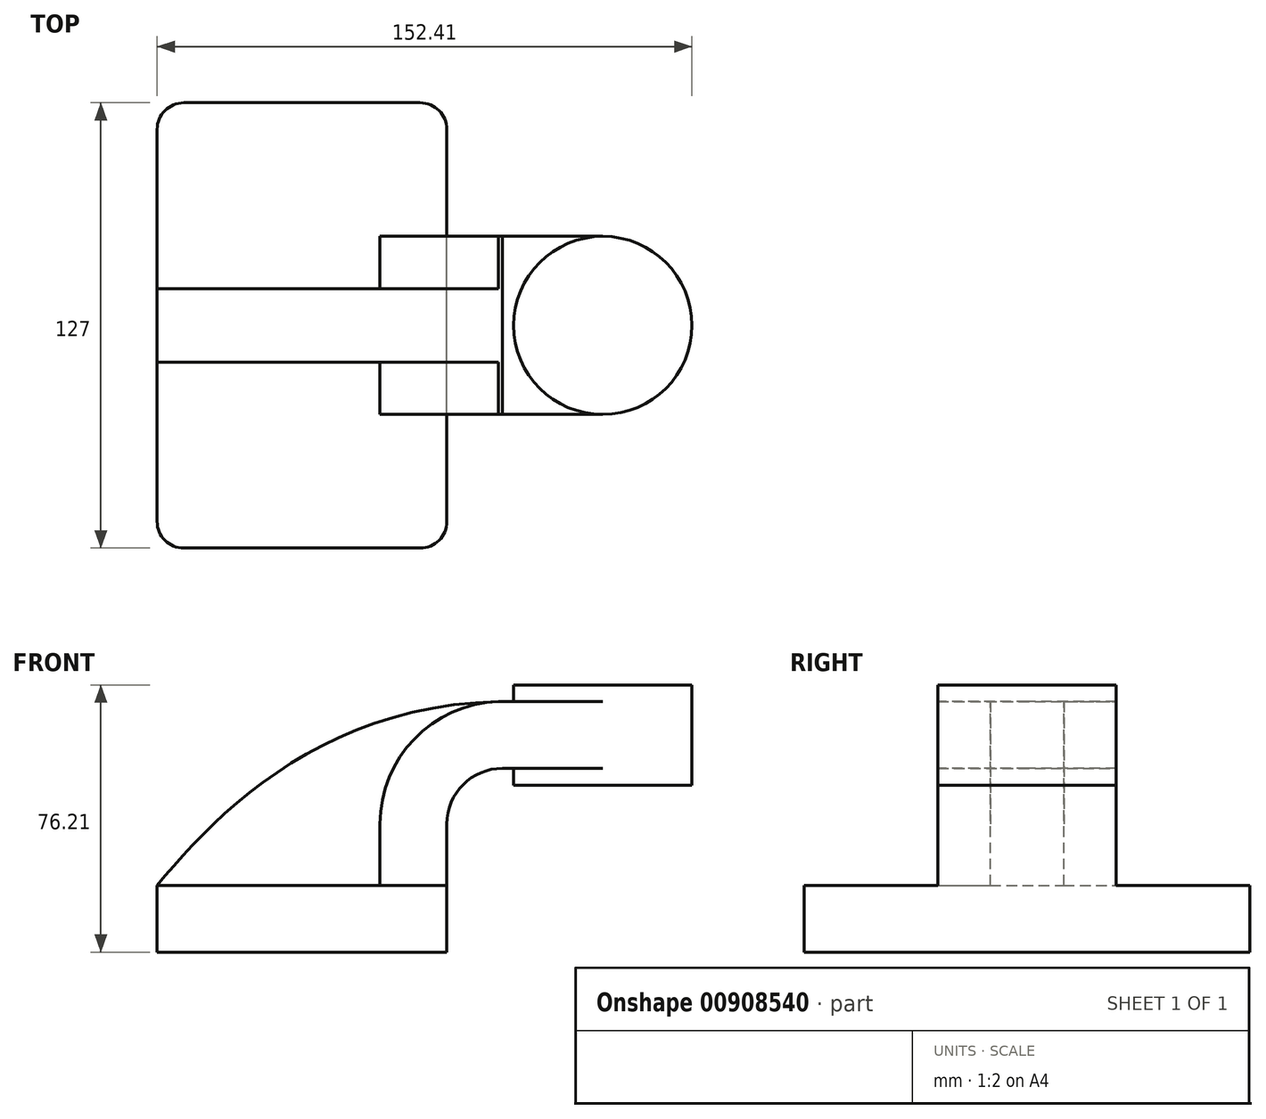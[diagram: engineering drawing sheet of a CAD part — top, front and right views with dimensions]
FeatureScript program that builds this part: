
annotation { "Feature Type Name" : "Feature", "Feature Type Description" : "" }
export const myFeature = defineFeature(function(context is Context, id is Id, definition is map)
    precondition{}
    {
        {
            var Q0;
            Q0=qCreatedBy(makeId("Front.planeOp"),FACE);
            var sketch = newSketch(context, id + "F0", { "sketchPlane" : qUnion([Q0])});
            skLineSegment(sketch, "E0.bottom", {"start": v(41.28, -9.52) * mm, "end": v(-41.28, -9.53) * mm});
            skLineSegment(sketch, "E0.top", {"start": v(41.27, 9.53) * mm, "end": v(-41.28, 9.53) * mm});
            skLineSegment(sketch, "E0.left", {"start": v(41.28, -9.52) * mm, "end": v(41.28, 9.53) * mm});
            skLineSegment(sketch, "E0.right", {"start": v(-41.28, -9.53) * mm, "end": v(-41.28, 9.53) * mm});
            skPoint(sketch, "E0.middle", {"position": v(0, 0) * mm});
            skLineSegment(sketch, "E1.bottom", {"start": v(60.32, 66.68) * mm, "end": v(111.12, 66.68) * mm});
            skLineSegment(sketch, "E1.top", {"start": v(60.32, 38.1) * mm, "end": v(111.12, 38.1) * mm});
            skLineSegment(sketch, "E1.left", {"start": v(60.32, 66.68) * mm, "end": v(60.32, 38.1) * mm});
            skLineSegment(sketch, "E1.right", {"start": v(111.12, 66.68) * mm, "end": v(111.12, 38.1) * mm});
            skPoint(sketch, "E1.middle", {"position": v(85.72, 52.39) * mm});
            skLineSegment(sketch, "E2", {"start": v(41.27, 9.53) * mm, "end": v(41.27, 27) * mm});
            skArc(sketch, "E3", {"start": v(57.15, 42.88) * mm, "mid": v(45.92, 38.23) * mm, "end": v(41.27, 27) * mm});
            skLineSegment(sketch, "E4", {"start": v(57.15, 42.88) * mm, "end": v(85.72, 42.88) * mm});
            skLineSegment(sketch, "E5.0", {"start": v(57.15, 61.93) * mm, "end": v(85.72, 61.93) * mm});
            skArc(sketch, "E5.1", {"start": v(57.15, 61.93) * mm, "mid": v(32.45, 51.7) * mm, "end": v(22.23, 27) * mm});
            skLineSegment(sketch, "E5.2", {"start": v(22.22, 9.53) * mm, "end": v(22.22, 27) * mm});
            skLineSegment(sketch, "E6", {"start": v(85.72, 38.1) * mm, "end": v(85.72, 66.68) * mm});
            skFitSpline(sketch, "E7", {"points": [v(-41.28, 9.52) * mm, v(57.15, 61.93) * mm], "startDerivative": vector(51.54, 62.19) * mm, "endDerivative": vector(153.31, 1.88) * mm});
            skSolve(sketch);
        }
        {
            var Q0;
            Q0=makeQuery(id+"F0.imprint","IMPRINT",FACE,{"disambiguationData":[TD([[makeQuery(id+"F0.imprint","IMPRINT",EDGE,{"derivedFrom":sQuery(id+"F0.wireOp",EDGE,"E0.bottom")}),-1.0]])]});
            extrude(context, id + "F1", {"entities" : qUnion([Q0]), "endBound" : BoundingType.SYMMETRIC, "depth" : 127 * mm, "offsetDistance" : 25.4 * mm});
        }
        {
            var Q0;
            {var subQ3=sQuery(id+"F0.wireOp",EDGE,"E5.2");Q0=makeQuery(id+"F0.imprint","IMPRINT",FACE,{"disambiguationData":[TD([[makeQuery(id+"F0.imprint","IMPRINT",EDGE,{"derivedFrom":subQ3}),1.0]])]});}
            extrude(context, id + "F2", {"entities" : qUnion([Q0]), "operationType" : NewBodyOperationType.ADD, "endBound" : BoundingType.SYMMETRIC, "depth" : 20.95 * mm, "offsetDistance" : 25.4 * mm});
        }
        {
            var Q0;
            {var subQ1=sQuery(id+"F0.wireOp",EDGE,"E2");Q0=makeQuery(id+"F0.imprint","IMPRINT",FACE,{"disambiguationData":[TD([[makeQuery(id+"F0.imprint","IMPRINT",EDGE,{"derivedFrom":subQ1}),1.0]])]});}
            var Q1;
            {var subQ0=sQuery(id+"F0.wireOp",EDGE,"E5.0");var subQ1=sQuery(id+"F0.wireOp",EDGE,"E1.left");var subQ2=makeQuery(id+"F0.imprint","INTERSECT",VERTEX,{"derivedFrom":[subQ1,subQ0]});Q1=makeQuery(id+"F0.imprint","IMPRINT",FACE,{"disambiguationData":[TD([[makeQuery(id+"F0.imprint","IMPRINT",EDGE,{"disambiguationData":[TD([[subQ2,-1.0]])],"derivedFrom":subQ1}),1.0]])]});}
            extrude(context, id + "F3", {"entities" : qUnion([Q0, Q1]), "operationType" : NewBodyOperationType.ADD, "endBound" : BoundingType.SYMMETRIC, "depth" : 50.8 * mm, "offsetDistance" : 25.4 * mm});
        }
        {
            var Q0;
            {var subQ4=sQuery(id+"F0.wireOp",EDGE,"E1.right");Q0=makeQuery(id+"F0.imprint","IMPRINT",FACE,{"disambiguationData":[TD([[makeQuery(id+"F0.imprint","IMPRINT",EDGE,{"derivedFrom":subQ4}),-1.0]])]});}
            var Q1;
            Q1=sQuery(id+"F0.wireOp",EDGE,"E6");
            revolve(context, id + "F4", {"operationType" : NewBodyOperationType.ADD, "surfaceOperationType" : NewSurfaceOperationType.NEW, "entities" : qUnion([Q0]), "axis" : qUnion([Q1]), "revolveType" : RevolveType.FULL});
        }
        {
            var Q0;
            Q0=makeQuery(id+"F1.opExtrude","CAP_EDGE",EDGE,{"disambiguationData":[OSD([sQuery(id+"F0.wireOp",EDGE,"E0.left")])],"isStart":false});
            var Q1;
            Q1=makeQuery(id+"F1.opExtrude","CAP_EDGE",EDGE,{"disambiguationData":[OSD([sQuery(id+"F0.wireOp",EDGE,"E0.right")])],"isStart":false});
            var Q2;
            Q2=makeQuery(id+"F1.opExtrude","CAP_EDGE",EDGE,{"disambiguationData":[OSD([sQuery(id+"F0.wireOp",EDGE,"E0.left")])],"isStart":true});
            var Q3;
            Q3=makeQuery(id+"F1.opExtrude","CAP_EDGE",EDGE,{"disambiguationData":[OSD([sQuery(id+"F0.wireOp",EDGE,"E0.right")])],"isStart":true});
            fillet(context, id + "F5", {"entities" : qUnion([Q0, Q1, Q2, Q3]), "radius" : 7.62 * mm, "tangentPropagation" : true, "allowEdgeOverflow" : false});
        }
    });
